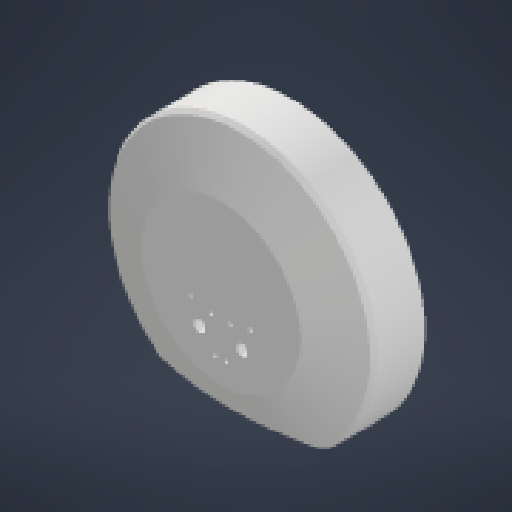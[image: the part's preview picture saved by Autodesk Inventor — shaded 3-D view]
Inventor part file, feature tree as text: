
AUTODESK INVENTOR PART (.ipt)
format: ipt  version: 2024 (Build 280153000, 153)  size: 111,616 bytes
history: native  units: in
note: dims shown in document units (in); Inventor stores cm internally (conversion verified against a paired STEP export)
features: other x3, sketch x1, reference x1
ambient origin geometry x8: Origin, YZ Plane, XZ Plane, XY Plane, X Axis, Y Axis, Z Axis, Center Point
feature tree (5):
  sketch  "Sketch1"  dims[d0=14.0in]
  reference  "Reference1"
  other  "<userpath>\Desktop\Camera_Mount.iam"
  other  "Camera_Mount.iam"
  other  "Head_Baseplate:1"
